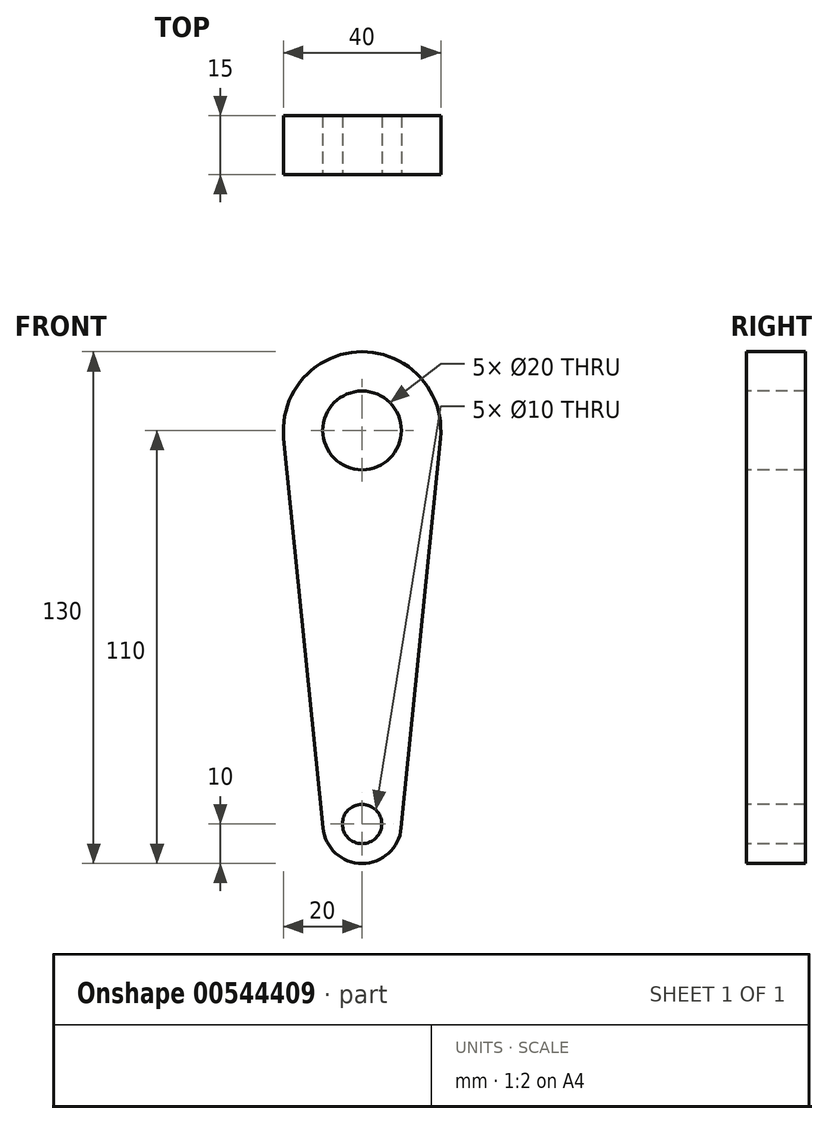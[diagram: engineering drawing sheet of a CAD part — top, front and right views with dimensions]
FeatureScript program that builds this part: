
annotation { "Feature Type Name" : "Feature", "Feature Type Description" : "" }
export const myFeature = defineFeature(function(context is Context, id is Id, definition is map)
    precondition{}
    {
        {
            var Q0;
            Q0=qCreatedBy(makeId("Front.planeOp"),FACE);
            var sketch = newSketch(context, id + "F0", { "sketchPlane" : qUnion([Q0])});
            skArc(sketch, "E0", {"start": v(19.9, -2) * mm, "mid": v(0, 20) * mm, "end": v(-19.9, -2) * mm});
            skArc(sketch, "E1", {"start": v(-9.95, -101) * mm, "mid": v(0, -110) * mm, "end": v(9.95, -101) * mm});
            skLineSegment(sketch, "E2", {"start": v(19.9, -2) * mm, "end": v(9.95, -101) * mm});
            skLineSegment(sketch, "E3.MirrorCS", {"start": v(-19.9, -2) * mm, "end": v(-9.95, -101) * mm});
            skSolve(sketch);
        }
        {
            var Q0;
            Q0=makeQuery(id+"F0.imprint","IMPRINT",FACE,{"disambiguationData":[TD([[makeQuery(id+"F0.imprint","IMPRINT",EDGE,{"derivedFrom":sQuery(id+"F0.wireOp",EDGE,"E0")}),1.0]])]});
            extrude(context, id + "F1", {"entities" : qUnion([Q0]), "endBound" : BoundingType.SYMMETRIC, "depth" : 15 * mm, "offsetDistance" : 25 * mm});
        }
        {
            var Q0;
            Q0=makeQuery(id+"F1.opExtrude","CAP_FACE",FACE,{"disambiguationData":[OSD([sQuery(id+"F0.wireOp",EDGE,"E0"),sQuery(id+"F0.wireOp",EDGE,"E1"),sQuery(id+"F0.wireOp",EDGE,"E2"),sQuery(id+"F0.wireOp",EDGE,"E3.MirrorCS")])],"isStart":false});
            var sketch = newSketch(context, id + "F2", { "sketchPlane" : qUnion([Q0])});
            skLineSegment(sketch, "E4", {"start": v(0, 0) * mm, "end": v(0, -100) * mm, "construction": true});
            skSolve(sketch);
        }
        {
            var Q0;
            Q0=sQuery(id+"F2.wireOp",VERTEX,"E4.start");
            var Q1;
            Q1=makeQuery(id+"F1.opExtrude","SWEPT_BODY",BODY,{"disambiguationData":[OSD([sQuery(id+"F0.wireOp",EDGE,"E0"),sQuery(id+"F0.wireOp",EDGE,"E1"),sQuery(id+"F0.wireOp",EDGE,"E2"),sQuery(id+"F0.wireOp",EDGE,"E3.MirrorCS")])]});
            hole(context, id + "F3", {"style" : HoleStyle.SIMPLE, "endStyle" : HoleEndStyle.THROUGH, "standardTappedOrClearance" : lookupTablePath({ "standard" : "ISO", "size" : "20", "type" : "Drilled" }), "standardBlindInLast" : lookupTablePath({ "standard" : "ISO", "size" : "20", "type" : "Drilled" }), "holeDiameter" : 20 * mm, "isTappedThrough" : true, "tappedDepth" : 12 * mm, "tapClearance" : 3, "locations" : qUnion([Q0]), "scope" : qUnion([Q1])});
        }
        {
            var Q0;
            Q0=sQuery(id+"F2.wireOp",VERTEX,"E4.end");
            var Q1;
            Q1=makeQuery(id+"F1.opExtrude","SWEPT_BODY",BODY,{"disambiguationData":[OSD([sQuery(id+"F0.wireOp",EDGE,"E0"),sQuery(id+"F0.wireOp",EDGE,"E1"),sQuery(id+"F0.wireOp",EDGE,"E2"),sQuery(id+"F0.wireOp",EDGE,"E3.MirrorCS")])]});
            hole(context, id + "F4", {"style" : HoleStyle.SIMPLE, "endStyle" : HoleEndStyle.THROUGH, "standardTappedOrClearance" : lookupTablePath({ "standard" : "ISO", "size" : "10", "type" : "Drilled" }), "standardBlindInLast" : lookupTablePath({ "standard" : "ISO", "size" : "10", "type" : "Drilled" }), "holeDiameter" : 10 * mm, "isTappedThrough" : true, "tappedDepth" : 12 * mm, "tapClearance" : 3, "locations" : qUnion([Q0]), "scope" : qUnion([Q1])});
        }
    });
